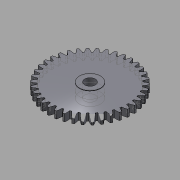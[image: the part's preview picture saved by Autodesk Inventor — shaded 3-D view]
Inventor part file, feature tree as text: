
AUTODESK INVENTOR PART (.ipt)
format: ipt  version: 2015 (Build 190159000, 159)  size: 347,648 bytes
history: native  units: in
note: dims shown in document units (in); Inventor stores cm internally (conversion verified against a paired STEP export)
features: other x13, sketch x5, plane x2
ambient origin geometry x8: Origin, YZ Plane, XZ Plane, XY Plane, X Axis, Y Axis, Z Axis, Center Point
bodies: Solid1 (feature_tree)
feature tree (20):
  other  "Spur Gear28_MIR1.ipt"
  other  "Solid1::Spur Gear28_MIR1.ipt"
  other  "TaggingFeature1"
  sketch  "Sketch1"  dims[d0=0.3937in]
  sketch  "Sketch2"  dims[d16=0.5709in d17=0.0in d41=0.0in d43=0.5709in d46=0.5709in d47=0.0in d48=0.0in]
  sketch  "Sketch3"
  sketch  "Sketch4"
  sketch  "Sketch5"
  plane  "XZ Plane_1"
  plane  "Work Plane2"
  other  "Z Axis_1"
  other  "Srf1"
  other  "Srf1::Derived"
  other  "Distance iMate"
  other  "Align iMate"
  other  "Mesh iMate"
  other  "Axis iMate"
  other  "Position iMate"
  other  "Mesh iMate2"
  other  "Start plane iMate"
